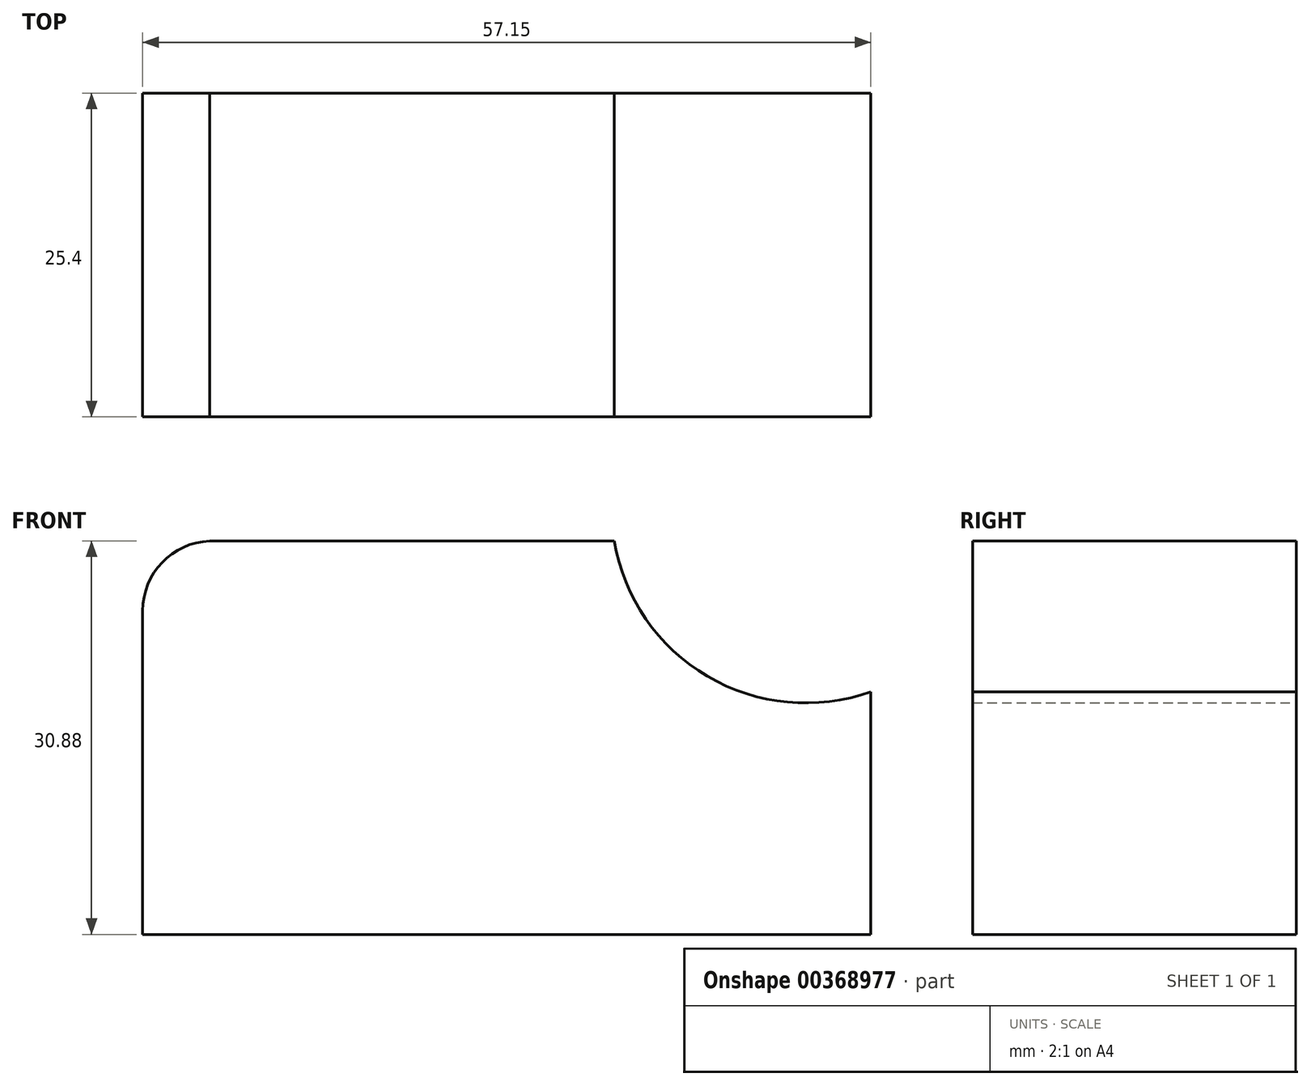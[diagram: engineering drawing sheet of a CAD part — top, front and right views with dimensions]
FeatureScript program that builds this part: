
annotation { "Feature Type Name" : "Feature", "Feature Type Description" : "" }
export const myFeature = defineFeature(function(context is Context, id is Id, definition is map)
    precondition{}
    {
        {
            var Q0;
            Q0=qCreatedBy(makeId("Front.planeOp"),FACE);
            var sketch = newSketch(context, id + "F0", { "sketchPlane" : qUnion([Q0])});
            skLineSegment(sketch, "E0", {"start": v(2.2, 0) * mm, "end": v(59.34, 0) * mm});
            skLineSegment(sketch, "E1", {"start": v(59.34, 0) * mm, "end": v(59.34, 19.05) * mm});
            skLineSegment(sketch, "E2", {"start": v(2.2, 0) * mm, "end": v(2.2, 25.4) * mm});
            skLineSegment(sketch, "E3", {"start": v(7.46, 30.88) * mm, "end": v(39.2, 30.88) * mm});
            skArc(sketch, "E4", {"start": v(2.2, 25.4) * mm, "mid": v(3.72, 29.2) * mm, "end": v(7.46, 30.88) * mm});
            skArc(sketch, "E5", {"start": v(39.2, 30.88) * mm, "mid": v(46.51, 20.26) * mm, "end": v(59.34, 19.05) * mm});
            skSolve(sketch);
        }
        {
            var Q0;
            Q0=makeQuery(id+"F0.imprint","IMPRINT",FACE,{"disambiguationData":[TD([[makeQuery(id+"F0.imprint","IMPRINT",EDGE,{"derivedFrom":sQuery(id+"F0.wireOp",EDGE,"E0")}),1.0]])]});
            extrude(context, id + "F1", {"entities" : qUnion([Q0]), "depth" : 25.4 * mm});
        }
    });
